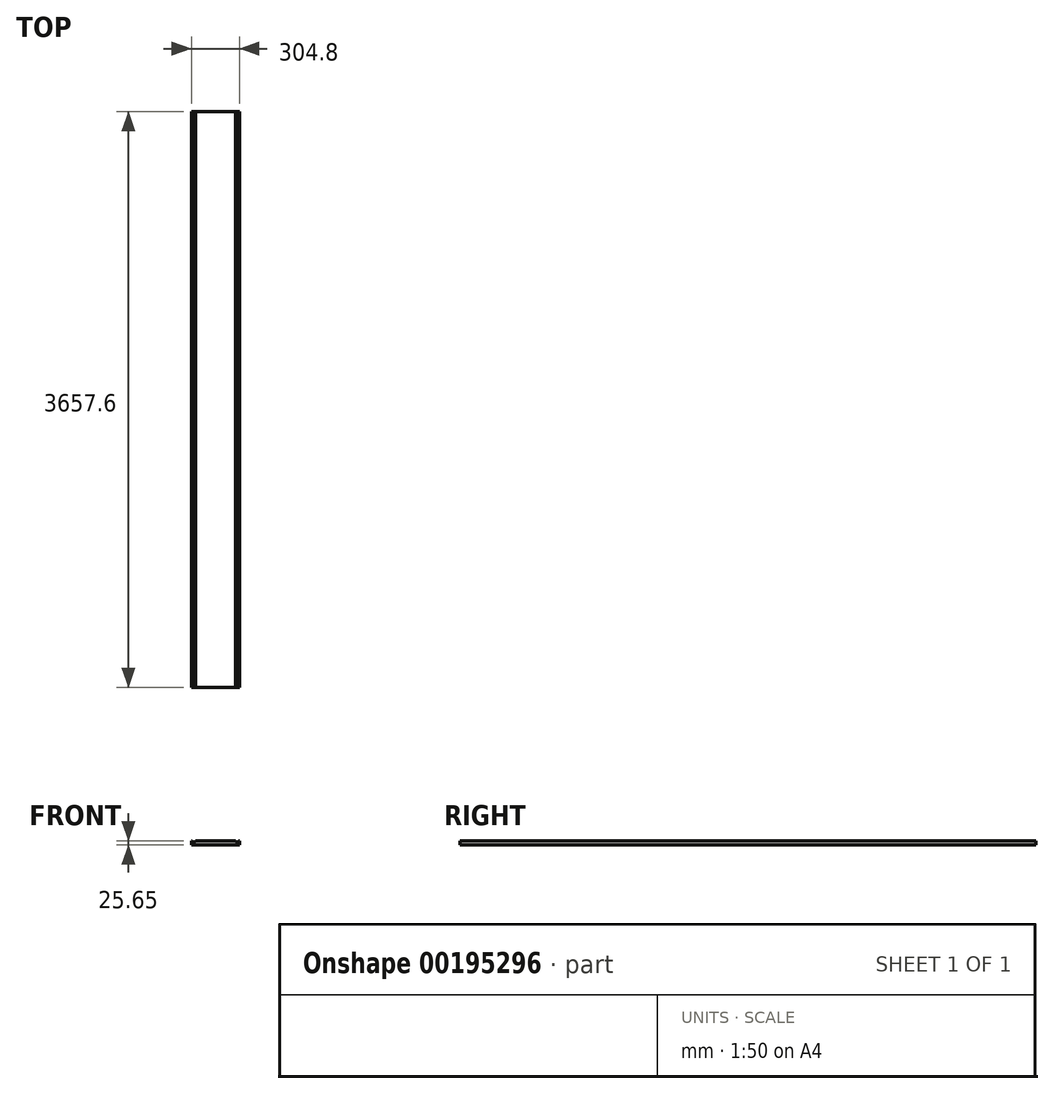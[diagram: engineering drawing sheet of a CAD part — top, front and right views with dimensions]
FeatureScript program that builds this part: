
annotation { "Feature Type Name" : "Feature", "Feature Type Description" : "" }
export const myFeature = defineFeature(function(context is Context, id is Id, definition is map)
    precondition{}
    {
        {
            var Q0;
            Q0=qCreatedBy(makeId("Front.planeOp"),FACE);
            var sketch = newSketch(context, id + "F0", { "sketchPlane" : qUnion([Q0])});
            skLineSegment(sketch, "E0.bottom", {"start": v(-47.76, 14.58) * mm, "end": v(257.04, 14.58) * mm});
            skLineSegment(sketch, "E0.top", {"start": v(-47.76, -11.07) * mm, "end": v(257.04, -11.07) * mm});
            skLineSegment(sketch, "E0.left", {"start": v(-47.76, 14.58) * mm, "end": v(-47.76, -11.07) * mm});
            skLineSegment(sketch, "E0.right", {"start": v(257.04, 14.58) * mm, "end": v(257.04, -11.07) * mm});
            skLineSegment(sketch, "E1", {"start": v(-41.66, 14.58) * mm, "end": v(-41.66, -11.07) * mm});
            skLineSegment(sketch, "E2", {"start": v(231.64, 14.58) * mm, "end": v(231.64, -11.07) * mm});
            skLineSegment(sketch, "E3", {"start": v(250.95, 14.58) * mm, "end": v(250.95, -11.07) * mm});
            skLineSegment(sketch, "E4", {"start": v(-22.36, 14.58) * mm, "end": v(-22.36, -11.07) * mm});
            skLineSegment(sketch, "E5", {"start": v(-41.66, 8.23) * mm, "end": v(-22.36, 8.23) * mm});
            skLineSegment(sketch, "E6", {"start": v(231.64, 8.23) * mm, "end": v(250.95, 8.23) * mm});
            skSolve(sketch);
        }
        {
            var Q0;
            Q0 = qSketchRegion(id + "F0", true);
            extrude(context, id + "F1", {"entities" : qUnion([Q0]), "oppositeDirection" : true, "depth" : 3657.6 * mm});
        }
        {
            var Q0;
            {var subQ5=sQuery(id+"F0.wireOp",EDGE,"E5");Q0=makeQuery(id+"F0.imprint","IMPRINT",FACE,{"disambiguationData":[TD([[makeQuery(id+"F0.imprint","IMPRINT",EDGE,{"derivedFrom":subQ5}),1.0]])]});}
            var sketch = newSketch(context, id + "F2", { "sketchPlane" : qUnion([Q0])});
            skSolve(sketch);
        }
        {
            var Q0;
            {var subQ5=sQuery(id+"F0.wireOp",EDGE,"E5");Q0=makeQuery(id+"F2.imprint","IMPRINT",FACE,{"disambiguationData":[TD([[makeQuery(id+"F2.imprint","IMPRINT",EDGE,{"derivedFrom":makeQuery(id+"F0.imprint","IMPRINT",EDGE,{"derivedFrom":subQ5})}),1.0]])]});}
            var Q1;
            {var subQ5=sQuery(id+"F0.wireOp",EDGE,"E6");Q1=makeQuery(id+"F0.imprint","IMPRINT",FACE,{"disambiguationData":[TD([[makeQuery(id+"F0.imprint","IMPRINT",EDGE,{"derivedFrom":subQ5}),1.0]])]});}
            extrude(context, id + "F3", {"entities" : qUnion([Q0, Q1]), "operationType" : NewBodyOperationType.REMOVE, "endBound" : BoundingType.THROUGH_ALL, "oppositeDirection" : true, "depth" : 25.4 * mm});
        }
    });
